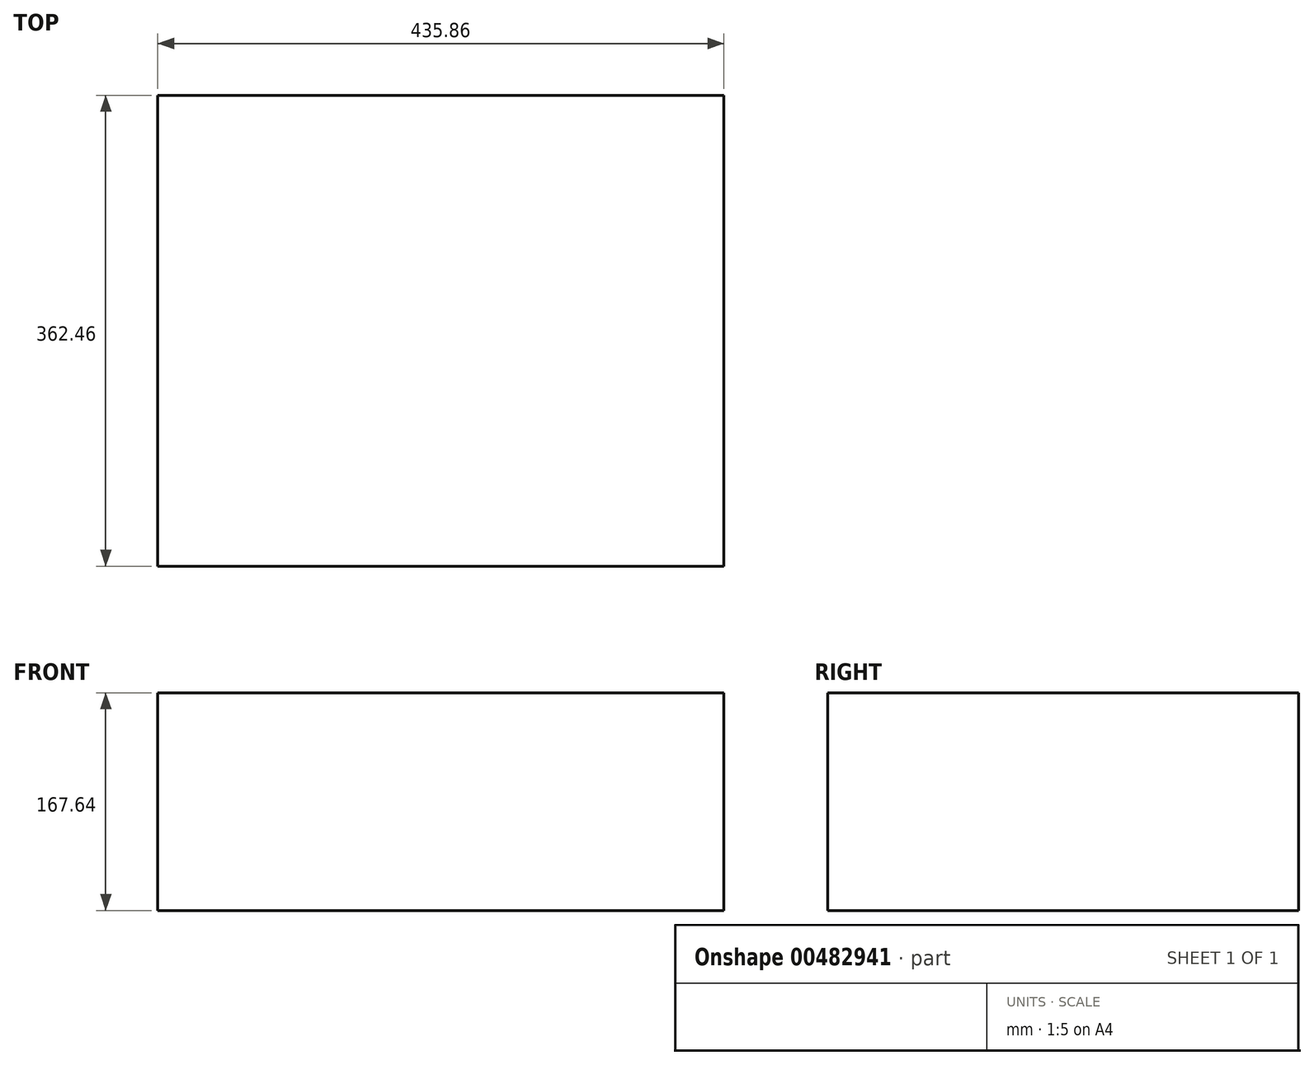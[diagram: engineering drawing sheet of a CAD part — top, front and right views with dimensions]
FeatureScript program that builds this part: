
annotation { "Feature Type Name" : "Feature", "Feature Type Description" : "" }
export const myFeature = defineFeature(function(context is Context, id is Id, definition is map)
    precondition{}
    {
        {
            var Q0;
            Q0=qCreatedBy(makeId("Top.planeOp"),FACE);
            var sketch = newSketch(context, id + "F0", { "sketchPlane" : qUnion([Q0])});
            skLineSegment(sketch, "E0.bottom", {"start": v(217.93, -181.23) * mm, "end": v(-217.93, -181.23) * mm});
            skLineSegment(sketch, "E0.top", {"start": v(217.93, 181.23) * mm, "end": v(-217.93, 181.23) * mm});
            skLineSegment(sketch, "E0.left", {"start": v(217.93, -181.23) * mm, "end": v(217.93, 181.23) * mm});
            skLineSegment(sketch, "E0.right", {"start": v(-217.93, -181.23) * mm, "end": v(-217.93, 181.23) * mm});
            skPoint(sketch, "E0.middle", {"position": v(0, 0) * mm});
            skSolve(sketch);
        }
        {
            var Q0;
            Q0=makeQuery(id+"F0.imprint","IMPRINT",FACE,{"disambiguationData":[TD([[makeQuery(id+"F0.imprint","IMPRINT",EDGE,{"derivedFrom":sQuery(id+"F0.wireOp",EDGE,"E0.bottom")}),-1.0]])]});
            extrude(context, id + "F1", {"entities" : qUnion([Q0]), "depth" : 167.64 * mm});
        }
    });
